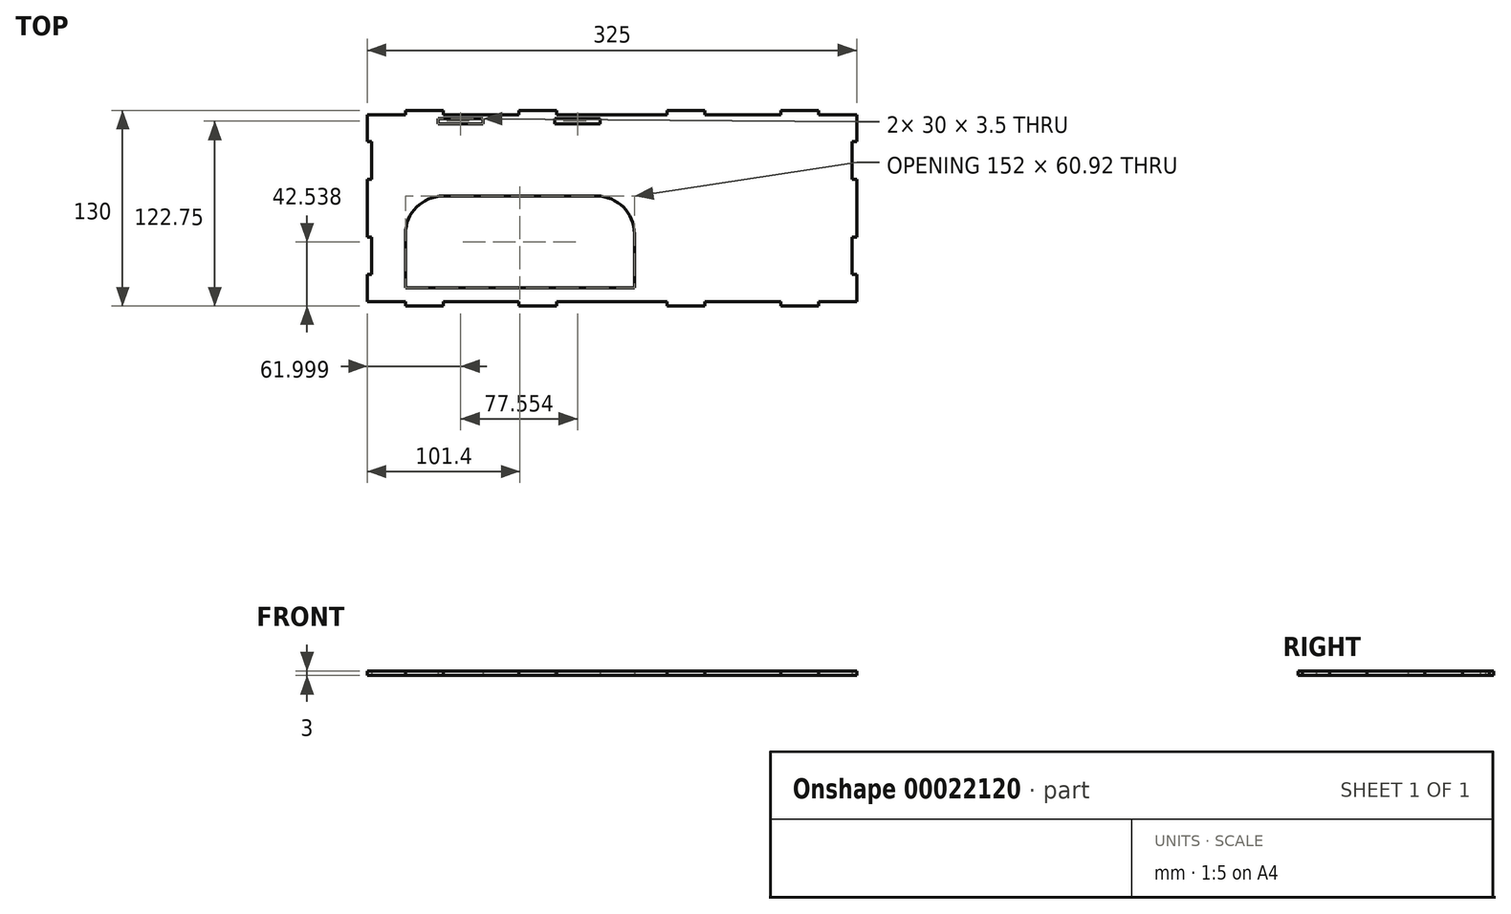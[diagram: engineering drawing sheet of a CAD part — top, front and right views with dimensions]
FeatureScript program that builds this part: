
annotation { "Feature Type Name" : "Feature", "Feature Type Description" : "" }
export const myFeature = defineFeature(function(context is Context, id is Id, definition is map)
    precondition{}
    {
        {
            var Q0;
            Q0=qCreatedBy(makeId("Top.planeOp"),FACE);
            var sketch = newSketch(context, id + "F0", { "sketchPlane" : qUnion([Q0])});
            skLineSegment(sketch, "E0.left", {"start": v(-137.13, 5) * mm, "end": v(-137.13, 2) * mm});
            skLineSegment(sketch, "E0.right", {"start": v(-112.13, 5) * mm, "end": v(-112.13, 2) * mm});
            skLineSegment(sketch, "E1.left", {"start": v(-61.72, 5) * mm, "end": v(-61.72, 2) * mm});
            skLineSegment(sketch, "E1.right", {"start": v(-36.72, 5) * mm, "end": v(-36.72, 2) * mm});
            skLineSegment(sketch, "E2.MirrorCS", {"start": v(61.72, 5) * mm, "end": v(61.72, 2) * mm});
            skLineSegment(sketch, "E3.MirrorCS", {"start": v(36.72, 5) * mm, "end": v(36.72, 2) * mm});
            skLineSegment(sketch, "E4.MirrorCS", {"start": v(137.13, 5) * mm, "end": v(137.13, 2) * mm});
            skLineSegment(sketch, "E5.MirrorCS", {"start": v(112.13, 5) * mm, "end": v(112.13, 2) * mm});
            skLineSegment(sketch, "E6.MirrorCS", {"start": v(-137.13, -125) * mm, "end": v(-137.13, -122) * mm});
            skLineSegment(sketch, "E7.MirrorCS", {"start": v(-112.13, -125) * mm, "end": v(-112.13, -122) * mm});
            skLineSegment(sketch, "E8.MirrorCS", {"start": v(-61.72, -125) * mm, "end": v(-61.72, -122) * mm});
            skLineSegment(sketch, "E9.MirrorCS", {"start": v(-36.72, -125) * mm, "end": v(-36.72, -122) * mm});
            skLineSegment(sketch, "E10.MirrorCS", {"start": v(36.72, -125) * mm, "end": v(36.72, -122) * mm});
            skLineSegment(sketch, "E11.MirrorCS", {"start": v(61.72, -125) * mm, "end": v(61.72, -122) * mm});
            skLineSegment(sketch, "E12.MirrorCS", {"start": v(112.13, -125) * mm, "end": v(112.13, -122) * mm});
            skLineSegment(sketch, "E13.MirrorCS", {"start": v(137.13, -125) * mm, "end": v(137.13, -122) * mm});
            skLineSegment(sketch, "E14", {"start": v(-162.5, 2) * mm, "end": v(-162.5, -15.9) * mm});
            skLineSegment(sketch, "E15", {"start": v(162.5, 2) * mm, "end": v(162.5, -15.9) * mm});
            skLineSegment(sketch, "E16", {"start": v(-162.5, -122) * mm, "end": v(-137.13, -122) * mm});
            skLineSegment(sketch, "E17", {"start": v(137.13, -125) * mm, "end": v(112.13, -125) * mm});
            skLineSegment(sketch, "E18", {"start": v(61.72, -125) * mm, "end": v(36.72, -125) * mm});
            skLineSegment(sketch, "E19", {"start": v(-36.72, -125) * mm, "end": v(-61.72, -125) * mm});
            skLineSegment(sketch, "E20", {"start": v(-112.13, -125) * mm, "end": v(-137.13, -125) * mm});
            skLineSegment(sketch, "E21.trimOffspring", {"start": v(-112.13, -122) * mm, "end": v(-61.72, -122) * mm});
            skLineSegment(sketch, "E22.trimOffspring", {"start": v(-36.72, -122) * mm, "end": v(36.72, -122) * mm});
            skLineSegment(sketch, "E23.trimOffspring", {"start": v(61.72, -122) * mm, "end": v(112.13, -122) * mm});
            skLineSegment(sketch, "E24.trimOffspring", {"start": v(137.13, -122) * mm, "end": v(162.5, -122) * mm});
            skPoint(sketch, "E25.MirrorCS.end.orphan", {"position": v(36.72, 2) * mm});
            skPoint(sketch, "E25.MirrorCS.start.orphan", {"position": v(61.72, 2) * mm});
            skPoint(sketch, "E26.MirrorCS.end.orphan", {"position": v(112.13, 2) * mm});
            skPoint(sketch, "E26.MirrorCS.start.orphan", {"position": v(137.13, 2) * mm});
            skLineSegment(sketch, "E27", {"start": v(137.13, 2) * mm, "end": v(162.5, 2) * mm});
            skLineSegment(sketch, "E28", {"start": v(137.13, 5) * mm, "end": v(112.13, 5) * mm});
            skLineSegment(sketch, "E29", {"start": v(112.13, 2) * mm, "end": v(61.72, 2) * mm});
            skLineSegment(sketch, "E30", {"start": v(61.72, 5) * mm, "end": v(36.72, 5) * mm});
            skLineSegment(sketch, "E31", {"start": v(36.72, 2) * mm, "end": v(-36.72, 2) * mm});
            skLineSegment(sketch, "E32", {"start": v(-36.72, 5) * mm, "end": v(-61.72, 5) * mm});
            skLineSegment(sketch, "E33", {"start": v(-61.72, 2) * mm, "end": v(-112.13, 2) * mm});
            skLineSegment(sketch, "E34", {"start": v(-112.13, 5) * mm, "end": v(-137.13, 5) * mm});
            skLineSegment(sketch, "E35", {"start": v(-137.13, 2) * mm, "end": v(-162.5, 2) * mm});
            skLineSegment(sketch, "E36.bottom", {"start": v(162.5, -15.9) * mm, "end": v(159.57, -15.9) * mm});
            skLineSegment(sketch, "E36.top", {"start": v(162.5, -40.76) * mm, "end": v(159.5, -40.76) * mm});
            skLineSegment(sketch, "E36.right", {"start": v(159.57, -15.9) * mm, "end": v(159.57, -40.76) * mm});
            skLineSegment(sketch, "E37.MirrorCS", {"start": v(159.57, -104.1) * mm, "end": v(159.57, -79.24) * mm});
            skLineSegment(sketch, "E38.MirrorCS", {"start": v(162.5, -79.24) * mm, "end": v(159.5, -79.24) * mm});
            skLineSegment(sketch, "E39.MirrorCS", {"start": v(162.5, -104.1) * mm, "end": v(159.57, -104.1) * mm});
            skLineSegment(sketch, "E40.trimOffspring", {"start": v(162.5, -104.1) * mm, "end": v(162.5, -122) * mm});
            skLineSegment(sketch, "E41.trimOffspring", {"start": v(162.5, -40.76) * mm, "end": v(162.5, -79.24) * mm});
            skLineSegment(sketch, "E42.MirrorCS", {"start": v(-159.57, -15.9) * mm, "end": v(-159.57, -40.76) * mm});
            skLineSegment(sketch, "E43.MirrorCS", {"start": v(-159.57, -104.1) * mm, "end": v(-159.57, -79.24) * mm});
            skLineSegment(sketch, "E44.MirrorCS", {"start": v(-162.5, -40.76) * mm, "end": v(-159.5, -40.76) * mm});
            skLineSegment(sketch, "E45.MirrorCS", {"start": v(-162.5, -15.9) * mm, "end": v(-159.57, -15.9) * mm});
            skLineSegment(sketch, "E46.MirrorCS", {"start": v(-162.5, -79.24) * mm, "end": v(-159.5, -79.24) * mm});
            skLineSegment(sketch, "E47.MirrorCS", {"start": v(-162.5, -104.1) * mm, "end": v(-159.57, -104.1) * mm});
            skLineSegment(sketch, "E48.trimOffspring", {"start": v(-162.5, -40.76) * mm, "end": v(-162.5, -79.24) * mm});
            skLineSegment(sketch, "E49.trimOffspring", {"start": v(-162.5, -104.1) * mm, "end": v(-162.5, -122) * mm});
            skLineSegment(sketch, "E50.bottom", {"start": v(-10.1, -52) * mm, "end": v(-112.1, -52) * mm});
            skPoint(sketch, "E51.visualSharp", {"position": v(-137.1, -52) * mm});
            skArc(sketch, "E51.filletArc", {"start": v(-112.1, -52) * mm, "mid": v(-129.78, -59.32) * mm, "end": v(-137.1, -77) * mm});
            skPoint(sketch, "E52.visualSharp", {"position": v(14.9, -52) * mm});
            skArc(sketch, "E52.filletArc", {"start": v(14.9, -77) * mm, "mid": v(7.58, -59.32) * mm, "end": v(-10.1, -52) * mm});
            skLineSegment(sketch, "E53.bottom", {"start": v(-115.5, -0.5) * mm, "end": v(-85.5, -0.5) * mm});
            skLineSegment(sketch, "E53.top", {"start": v(-115.5, -4) * mm, "end": v(-85.5, -4) * mm});
            skLineSegment(sketch, "E53.left", {"start": v(-115.5, -0.5) * mm, "end": v(-115.5, -4) * mm});
            skLineSegment(sketch, "E53.right", {"start": v(-85.5, -0.5) * mm, "end": v(-85.5, -4) * mm});
            skLineSegment(sketch, "E54", {"start": v(-61.72, -117) * mm, "end": v(-61.72, -52) * mm, "construction": true});
            skLineSegment(sketch, "E55.MirrorCS", {"start": v(-7.95, -4) * mm, "end": v(-37.95, -4) * mm});
            skLineSegment(sketch, "E56.MirrorCS", {"start": v(-7.95, -0.5) * mm, "end": v(-37.95, -0.5) * mm});
            skLineSegment(sketch, "E57.MirrorCS", {"start": v(-37.95, -0.5) * mm, "end": v(-37.95, -4) * mm});
            skLineSegment(sketch, "E58.MirrorCS", {"start": v(-7.95, -0.5) * mm, "end": v(-7.95, -4) * mm});
            skLineSegment(sketch, "E59", {"start": v(-137.1, -77) * mm, "end": v(-137.1, -112.92) * mm});
            skLineSegment(sketch, "E60", {"start": v(-137.1, -112.92) * mm, "end": v(14.9, -112.92) * mm});
            skLineSegment(sketch, "E61", {"start": v(14.9, -112.92) * mm, "end": v(14.9, -77) * mm});
            skSolve(sketch);
        }
        {
            var Q0;
            Q0=makeQuery(id+"F0.imprint","IMPRINT",FACE,{"disambiguationData":[TD([[makeQuery(id+"F0.imprint","IMPRINT",EDGE,{"derivedFrom":sQuery(id+"F0.wireOp",EDGE,"E0.left")}),1.0]])]});
            extrude(context, id + "F1", {"entities" : qUnion([Q0]), "depth" : 3 * mm});
        }
    });
